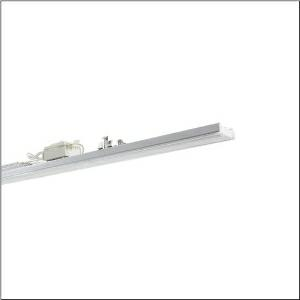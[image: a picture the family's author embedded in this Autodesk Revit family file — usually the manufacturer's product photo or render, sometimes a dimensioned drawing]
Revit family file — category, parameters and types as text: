
# Revit family: licross_r__11_recessed_extreme_ho_51te12dn4exme_c8ef
name_source: partatom
category: Lighting Fixtures
units: mm (PartAtom-declared; Revit-internal decimal feet)

## family parameters
Cut with Voids When Loaded = No
Host = Face
Light Source = No
Part Type = Normal
Room Calculation Point = No
Round Connector Dimension = Use Diameter
Shared = No

## types (1)
- --- (1 x LED, 14030 lm, 76.8 W, 4000K)
    Apparent Load = 77 VA
    CIE Flux Codes = 66 91 98 100 100
    Color Rendering = 80
    Color Temperature = 4000K
    Default Elevation = 1800 mm
    Description = Licross® 11 Recessed extreme HO, luminaire insert, of sheet steel, galvanised, coil coated, white, length: 1.500mm, width: 66mm, height: 67mm, LED rated luminous flux: 14.030lm, light colour: 840, control gear: DALI 2, with plug, 5-pole, with phase selection, mains connection: 220..240V, AC, 50/60Hz, rated input power: 77W, halogen-free wiring, primary optical cover: cover, of PMMA, light emission: direct distribution, primary light characteristic: symmetric, protection rating (complete): IP54, insulation class (complete): insulation class I (protective earthing), certification: CE, ENEC, VDE, UKCA, protection symbol: D if used in an environment with non-conductive dust loads with corresponding accessories, impact resistance: IK06, permissible ambient temperature for indoor applications: -40..+40°C, corresponds to IFS (International Featured Standards) requirements for safety and quality in the food industry, reducing of maximum allowable ambient temperature of 5°C with ceiling mounting, LABS conformity tested according to VDMA 24364:2018-05, packaging unit: 1 piece
    Height = 58 mm
    Lamp = 1 x LED
    Lamp Light Flux = 14030 lm
    Lamp Power = 76.8 W
    Lamp count = 1
    Length = 1500 mm
    Luminous efficacy = 183 lm/W
    Manufacturer = Siteco
    ModVariant = No
    Model = 51TE12DN4EXME
    Mounting Place = Ceiling
    Mounting Type = Pendant
    Number of Poles = 1
    OnlyDefault = Yes
    Power Factor = 1
    Product Name = Licross® 11 Recessed extreme HO
    Product group = luminaire insert
    ProductGroupID = 902
    Protection Class = Protection class I
    Protection Degree = IP 54
    RLX_Detail_Level = 1
    RLX_Emergency_Light_Flux = 0 lm
    RLX_Emergency_Type = 0
    RLX_Emergency_Type_DB = No
    RlxData = <blob elided: 24665 chars, md5=aac98dd1>
    Socket = socket
    Standby Power = 0 W
    System Light Flux = 14030 lm
    System Power = 77 W
    Type Comments = factory setting: luminous flux: 100 % | dim-lin: 254 | 522 mA
    Type Image = l_1296930.jpg
    URL = http://relux.com
    VarID = @adj_082362
    Voltage = 0 V
    Weight = 0.00 kg
    Width = 66 mm

## geometry (parser evidence)
native form markers: Blend x4, Sweep x12
no freeform markers — native parametric forms only
